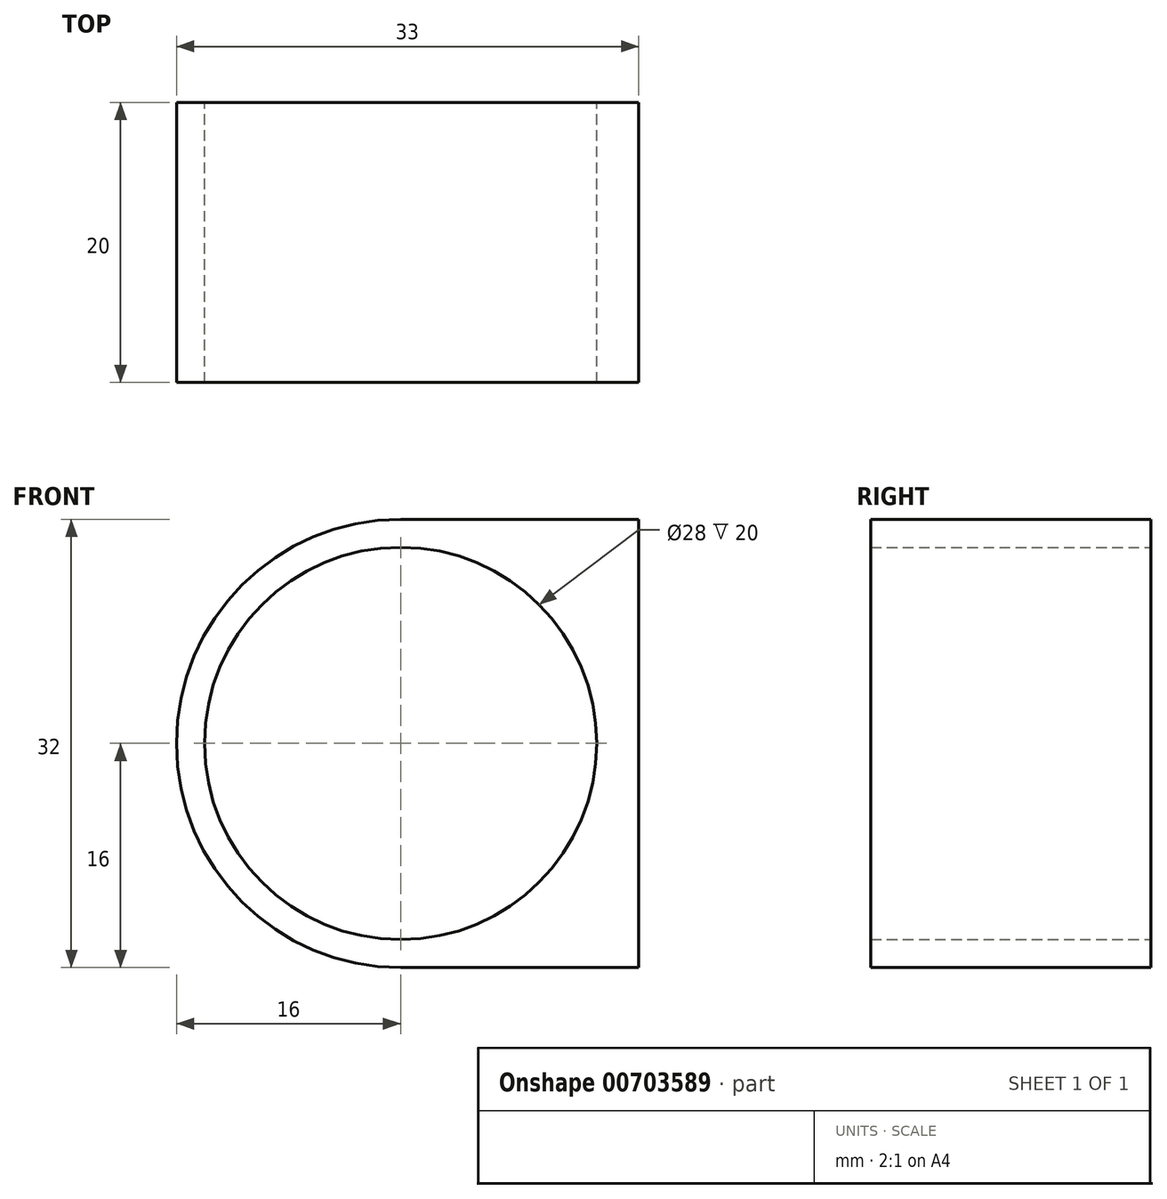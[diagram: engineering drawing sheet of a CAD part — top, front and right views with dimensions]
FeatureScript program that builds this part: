
annotation { "Feature Type Name" : "Feature", "Feature Type Description" : "" }
export const myFeature = defineFeature(function(context is Context, id is Id, definition is map)
    precondition{}
    {
        {
            var Q0;
            Q0=qCreatedBy(makeId("Front.planeOp"),FACE);
            var sketch = newSketch(context, id + "F0", { "sketchPlane" : qUnion([Q0])});
            skCircle(sketch, "E0", {"center": v(0, 0) * mm, "radius": 16 * mm});
            skCircle(sketch, "E1", {"center": v(0, 0) * mm, "radius": 10.5 * mm});
            skSolve(sketch);
        }
        {
            var Q0;
            Q0=qSketchRegion(id+"F0",true);
            extrude(context, id + "F1", {"entities" : qUnion([Q0]), "depth" : 20 * mm, "offsetDistance" : 25 * mm});
        }
        {
            var Q0;
            Q0=makeQuery(id+"F1.opExtrude","CAP_FACE",FACE,{"disambiguationData":[OSD([sQuery(id+"F0.wireOp",EDGE,"E0"),sQuery(id+"F0.wireOp",EDGE,"E1")])],"isStart":false});
            var sketch = newSketch(context, id + "F2", { "sketchPlane" : qUnion([Q0])});
            skCircle(sketch, "E2", {"center": v(0, 0) * mm, "radius": 12.5 * mm});
            skSolve(sketch);
        }
        {
            var Q0;
            Q0=qSketchRegion(id+"F2",true);
            extrude(context, id + "F3", {"entities" : qUnion([Q0]), "operationType" : NewBodyOperationType.ADD, "oppositeDirection" : true, "depth" : 15 * mm, "offsetDistance" : 25 * mm});
        }
        {
            var Q0;
            Q0=makeQuery(id+"F3.opExtrude","CAP_FACE",FACE,{"disambiguationData":[OSD([sQuery(id+"F2.wireOp",EDGE,"E2")])],"isStart":false});
            extrude(context, id + "F4", {"entities" : qUnion([Q0]), "operationType" : NewBodyOperationType.REMOVE, "endBound" : BoundingType.THROUGH_ALL, "oppositeDirection" : true, "depth" : 25 * mm, "offsetDistance" : 25 * mm});
        }
        {
            var Q0;
            Q0=makeQuery(id+"F1.opExtrude","CAP_FACE",FACE,{"disambiguationData":[OSD([sQuery(id+"F0.wireOp",EDGE,"E0"),sQuery(id+"F0.wireOp",EDGE,"E1")])],"isStart":true});
            var sketch = newSketch(context, id + "F5", { "sketchPlane" : qUnion([Q0])});
            skCircle(sketch, "E3", {"center": v(0, 0) * mm, "radius": 14 * mm});
            skSolve(sketch);
        }
        {
            var Q0;
            Q0=qSketchRegion(id+"F5",true);
            extrude(context, id + "F6", {"entities" : qUnion([Q0]), "operationType" : NewBodyOperationType.REMOVE, "oppositeDirection" : true, "depth" : 15 * mm, "offsetDistance" : 25 * mm});
        }
        {
            var Q0;
            Q0=qCreatedBy(makeId("Right.planeOp"),FACE);
            cPlane(context, id + "F7", {"entities" : qUnion([Q0]), "cplaneType" : CPlaneType.OFFSET, "offset" : 15 * mm, "width" : 150 * mm, "height" : 150 * mm});
        }
        {
            var Q0;
            Q0=qCreatedBy(id+"F7.planeOp",FACE);
            var sketch = newSketch(context, id + "F8", { "sketchPlane" : qUnion([Q0])});
            skLineSegment(sketch, "E4.bottom", {"start": v(0, 0) * mm, "end": v(-20, 0) * mm});
            skLineSegment(sketch, "E4.top", {"start": v(0, 16) * mm, "end": v(-20, 16) * mm});
            skLineSegment(sketch, "E4.left", {"start": v(0, 0) * mm, "end": v(0, 16) * mm});
            skLineSegment(sketch, "E4.right", {"start": v(-20, 0) * mm, "end": v(-20, 16) * mm});
            skLineSegment(sketch, "E5.top", {"start": v(0, -16) * mm, "end": v(-20, -16) * mm});
            skLineSegment(sketch, "E5.left", {"start": v(0, 0) * mm, "end": v(0, -16) * mm});
            skLineSegment(sketch, "E5.right", {"start": v(-20, 0) * mm, "end": v(-20, -16) * mm});
            skSolve(sketch);
        }
        {
            var Q0;
            Q0=qSketchRegion(id+"F8",true);
            extrude(context, id + "F9", {"entities" : qUnion([Q0]), "operationType" : NewBodyOperationType.ADD, "depth" : 2 * mm, "offsetDistance" : 25 * mm});
        }
        {
            var Q0;
            Q0=makeQuery(id+"F3.boolean.opBoolean","MERGE",FACE,{"derivedFrom":[makeQuery(id+"F1.opExtrude","CAP_FACE",FACE,{"disambiguationData":[OSD([sQuery(id+"F0.wireOp",EDGE,"E0"),sQuery(id+"F0.wireOp",EDGE,"E1")])],"isStart":false}),makeQuery(id+"F3.opExtrude","CAP_FACE",FACE,{"disambiguationData":[OSD([sQuery(id+"F2.wireOp",EDGE,"E2")])],"isStart":true})]});
            var sketch = newSketch(context, id + "F10", { "sketchPlane" : qUnion([Q0])});
            skLineSegment(sketch, "E6", {"start": v(0, 16) * mm, "end": v(15.98, 16) * mm});
            skLineSegment(sketch, "E7", {"start": v(0, -16) * mm, "end": v(16.04, -16) * mm});
            skSolve(sketch);
        }
        {
            var Q0;
            {var subQ1=sQuery(id+"F8.wireOp",EDGE,"E4.top");var subQ3=sQuery(id+"F8.wireOp",EDGE,"E5.right");var subQ4=sQuery(id+"F8.wireOp",EDGE,"E4.right");var subQ5=makeQuery(id+"F9.boolean.opBoolean","SPLIT",EDGE,{"disambiguationData":[TD([makeQuery(id+"F9.opExtrude","SWEPT_FACE",FACE,{"disambiguationData":[OSD([subQ1])]})])],"derivedFrom":makeQuery(id+"F9.opExtrude","CAP_EDGE",EDGE,{"disambiguationData":[OSD([subQ4,subQ3])],"isStart":true})});Q0=makeQuery(id+"F10.imprint","IMPRINT",FACE,{"disambiguationData":[TD([[makeQuery(id+"F10.imprint","IMPRINT",EDGE,{"derivedFrom":subQ5}),1.0]])]});}
            extrude(context, id + "F11", {"entities" : qUnion([Q0]), "operationType" : NewBodyOperationType.ADD, "oppositeDirection" : true, "depth" : 20 * mm, "offsetDistance" : 25 * mm});
        }
        {
            var Q0;
            {var subQ0=sQuery(id+"F8.wireOp",EDGE,"E5.right");var subQ1=sQuery(id+"F8.wireOp",EDGE,"E4.right");var subQ2=sQuery(id+"F0.wireOp",EDGE,"E0");Q0=makeQuery(id+"F11.boolean.opBoolean","MERGE",FACE,{"derivedFrom":[makeQuery(id+"F9.boolean.opBoolean","MERGE",FACE,{"derivedFrom":[makeQuery(id+"F3.boolean.opBoolean","MERGE",FACE,{"derivedFrom":[makeQuery(id+"F1.opExtrude","CAP_FACE",FACE,{"disambiguationData":[OSD([subQ2,sQuery(id+"F0.wireOp",EDGE,"E1")])],"isStart":false}),makeQuery(id+"F3.opExtrude","CAP_FACE",FACE,{"disambiguationData":[OSD([sQuery(id+"F2.wireOp",EDGE,"E2")])],"isStart":true})]}),makeQuery(id+"F9.opExtrude","SWEPT_FACE",FACE,{"disambiguationData":[OSD([subQ1,subQ0])]})]}),makeQuery(id+"F11.opExtrude","CAP_FACE",FACE,{"disambiguationData":[OSD([subQ2,subQ1,subQ0,sQuery(id+"F10.wireOp",EDGE,"E6")])],"isStart":true})]});}
            var sketch = newSketch(context, id + "F12", { "sketchPlane" : qUnion([Q0])});
            skSolve(sketch);
        }
        {
            var Q0;
            {var subQ3=sQuery(id+"F0.wireOp",EDGE,"E0");Q0=makeQuery(id+"F12.imprint","IMPRINT",FACE,{"disambiguationData":[TD([[makeQuery(id+"F12.imprint","IMPRINT",EDGE,{"derivedFrom":makeQuery(id+"F1.opExtrude","CAP_EDGE",EDGE,{"disambiguationData":[OSD([subQ3])],"isStart":false})}),1.0]])]});}
            var sketch = newSketch(context, id + "F13", { "sketchPlane" : qUnion([Q0])});
            skLineSegment(sketch, "E8", {"start": v(15, -16) * mm, "end": v(0, -16) * mm});
            skSolve(sketch);
        }
        {
            var Q0;
            Q0=qSketchRegion(id+"F13",true);
            var Q1;
            {var subQ0=sQuery(id+"F13.wireOp",EDGE,"E8");Q1=makeQuery(id+"F13.imprint","IMPRINT",FACE,{"disambiguationData":[TD([[makeQuery(id+"F13.imprint","IMPRINT",EDGE,{"derivedFrom":subQ0}),-1.0]])]});}
            extrude(context, id + "F14", {"entities" : qUnion([Q0, Q1]), "operationType" : NewBodyOperationType.ADD, "oppositeDirection" : true, "depth" : 20 * mm, "offsetDistance" : 25 * mm});
        }
        {
            var Q0;
            Q0=makeQuery(id+"F6.boolean.opBoolean","COPY",FACE,{"derivedFrom":makeQuery(id+"F6.opExtrude","CAP_FACE",FACE,{"disambiguationData":[OSD([sQuery(id+"F5.wireOp",EDGE,"E3")])],"isStart":false})});
            extrude(context, id + "F15", {"entities" : qUnion([Q0]), "operationType" : NewBodyOperationType.REMOVE, "endBound" : BoundingType.THROUGH_ALL, "oppositeDirection" : true, "depth" : 25 * mm, "offsetDistance" : 25 * mm});
        }
    });
